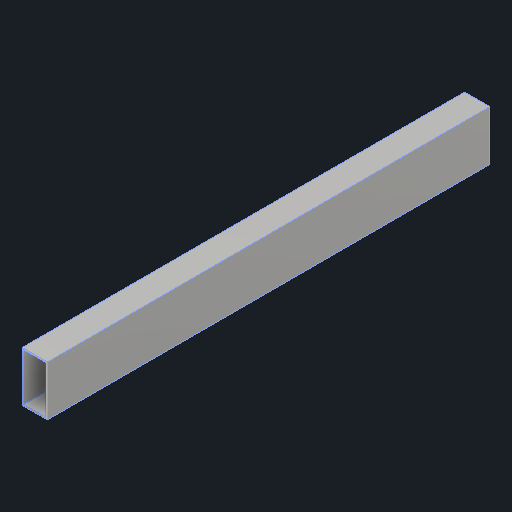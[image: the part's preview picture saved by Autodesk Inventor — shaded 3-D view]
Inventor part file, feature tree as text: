
AUTODESK INVENTOR PART (.ipt)
format: ipt  version: 2024.2 (Build 282272000, 272)  size: 236,544 bytes
history: native  units: in
note: dims shown in document units (in); Inventor stores cm internally (conversion verified against a paired STEP export)
features: extrude x1
ambient origin geometry x8: Origin, YZ Plane, XZ Plane, XY Plane, X Axis, Y Axis, Z Axis, Center Point
bodies: Solid1 (feature_tree)
feature tree (1):
  extrude  "Extrusion1"  TaperAngle=0.0deg  [1 undecoded]
note: 1 required parameter value undecoded (feature->parameter linkage not recoverable at this tier; creation-order binding heuristic only, values carry confidence <= 0.55)
